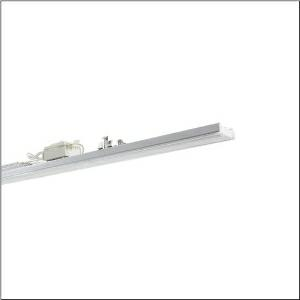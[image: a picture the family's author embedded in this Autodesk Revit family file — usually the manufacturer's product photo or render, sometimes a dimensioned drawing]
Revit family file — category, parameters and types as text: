
# Revit family: licross_r__21_recessed_ho_52tl12dn3exm_587e
name_source: partatom
category: Lighting Fixtures
units: mm (PartAtom-declared; Revit-internal decimal feet)

## family parameters
Cut with Voids When Loaded = No
Host = Face
Light Source = No
Part Type = Normal
Room Calculation Point = No
Round Connector Dimension = Use Diameter
Shared = No

## types (1)
- --- (1 x LED, 14040 lm, 84.6 W, 3000K)
    Apparent Load = 85 VA
    CIE Flux Codes = 69 91 98 100 100
    Color Rendering = 80
    Color Temperature = 3000K
    Default Elevation = 1800 mm
    Description = Licross® 21 Recessed HO, luminaire insert, of sheet steel, galvanised, coil coated, white, length: 1.500mm, width: 66mm, height: 67mm, LED rated luminous flux: 14.040lm, light colour: 830, control gear: DALI 2, with plug, 5-pole, with phase selection, mains connection: 220..240V, AC, 50/60Hz, rated input power: 85W, internal wiring halogen-free, primary optical cover: cover, of PMMA, light emission: direct distribution, primary light characteristic: symmetric, protection rating (complete): IP40, insulation class (complete): insulation class I (protective earthing), certification: CE, ENEC, VDE, UKCA, protection symbol: D if used in an environment without relevant dust loads with corresponding accessories, impact resistance: IK06, permissible ambient temperature for indoor applications: -25..+30°C, corresponds to IFS (International Featured Standards) requirements for safety and quality in the food industry, reducing of maximum allowable ambient temperature of 5°C with ceiling mounting, LABS conformity tested according to VDMA 24364:2018-05, packaging unit: 1 piece
    Height = 58 mm
    Lamp = 1 x LED
    Lamp Light Flux = 14040 lm
    Lamp Power = 84.6 W
    Lamp count = 1
    Length = 1500 mm
    Luminous efficacy = 166 lm/W
    Manufacturer = Siteco
    ModVariant = No
    Model = 52TL12DN3EXM
    Mounting Place = Ceiling
    Mounting Type = Pendant
    Number of Poles = 1
    OnlyDefault = Yes
    Power Factor = 1
    Product Name = Licross® 21 Recessed HO
    Product group = luminaire insert | ceiling pendant
    ProductGroupID = 902
    Protection Class = Protection class I
    Protection Degree = IP 40
    RLX_Detail_Level = 1
    RLX_Emergency_Light_Flux = 0 lm
    RLX_Emergency_Type = 0
    RLX_Emergency_Type_DB = No
    RlxData = <blob elided: 24725 chars, md5=7720e274>
    Socket = socket
    Standby Power = 0 W
    System Light Flux = 14040 lm
    System Power = 85 W
    Type Comments = factory setting: luminous flux: 100 % | dim-lin: 254 | 484 mA
    Type Image = l_1296930.jpg
    URL = http://relux.com
    VarID = @adj_110617
    Voltage = 0 V
    Weight = 0.00 kg
    Width = 66 mm

## geometry (parser evidence)
native form markers: Blend x4, Sweep x12
no freeform markers — native parametric forms only
